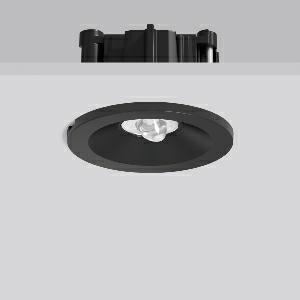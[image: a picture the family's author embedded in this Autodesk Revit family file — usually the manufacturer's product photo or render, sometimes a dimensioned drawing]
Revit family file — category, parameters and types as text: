
# Revit family: turia_l_672561_003_04_a44f
name_source: partatom
category: Lighting Fixtures
units: mm (PartAtom-declared; Revit-internal decimal feet)

## family parameters
Cut with Voids When Loaded = No
Host = Face
Light Source = No
Part Type = Normal
Room Calculation Point = No
Round Connector Dimension = Use Diameter
Shared = No

## types (1)
- TURIA L (1 x LED Modul 765, 240 lm, 6500)
    Apparent Load = 4 VA
    CIE Flux Codes = 70 91 99 100 100
    Color Rendering = 70
    Color Temperature = 6500
    Default Elevation = 1800 mm
    Description = Series: TURIA L
Round emergency luminaire for escape route lighting. Housing: die-cast aluminium. Bezel ring: plastic. With asymmetrical beam plastic lenses for illuminating rescue facilities. Self-contained system with automatic self-test and feedback to the RZB monitoring system MULTIDIGIT. With enclosed separate ceiling mounting ring also suitable for ceiling cut-outs of Ø 68 mm. 
Colour: black
Diameter: 62 mm
Height: 3 mm
Cut-out diameter: 54-68 mm
Recess height: 76-162 mm
Luminaire: recess height: 42 mm
Weight: 430 g
Operating mode: non-maintained power mode
Duration time: 3 h
Lamp: LED
Socket: without socket
Colour temperature: 6500K
Colour rendering index (CRI): 70
System power: 4.2 W
Rated luminous flux: 240 lm
Luminous flux, emergency: 170 lm
System power, emergency: -
Control gear: Regulated power supply
Protection class: II
Type of protection: IP 20
    Height = 0 mm  [stored 0 ft]
    Lamp = 1 x LED Modul 765
    Lamp Light Flux = 240 lm
    Lamp count = 1
    Length = 62 mm  [stored 0.203412 ft]
    Lifetime = 50000 h
    Luminous efficacy = 57 lm/W
    Manufacturer = RZB
    ModVariant = No
    Model = 672561.003.04
    Mounting Place = Ceiling
    Mounting Type = Recessed
    Number of Poles = 1
    OnlyDefault = Yes
    Power Factor = 1
    Product Name = TURIA L
    Product group = Recessed ceiling luminaires
    ProductGroupID = 405
    Protection Class = Protection class II
    Protection Degree = IP 20
    RLX_Detail_Level = 1
    RLX_Emergency_Light_Flux = 170 lm
    RLX_Emergency_Type = 3
    RLX_Emergency_Type_DB = Yes
    RlxData = <blob elided: 58049 chars, md5=f17c5418>
    Socket = socket
    Standby Power = 0 W
    System Light Flux = 240 lm
    System Power = 4 W
    Type Comments = Product without accessories
    Type Image = 672561.003.jpg
    URL = http://relux.com
    VarID = ---
    Voltage = 230 V
    Voltage Range = 220-240 V
    Weight = 0.00 kg
    Width = 0 mm  [stored 0 ft]

note: [stored X ft] marks values corroborated as IEEE doubles in the binary element streams (Revit-internal decimal feet)

## geometry (parser evidence)
native form markers: Blend x4, Sweep x11
no freeform markers — native parametric forms only
